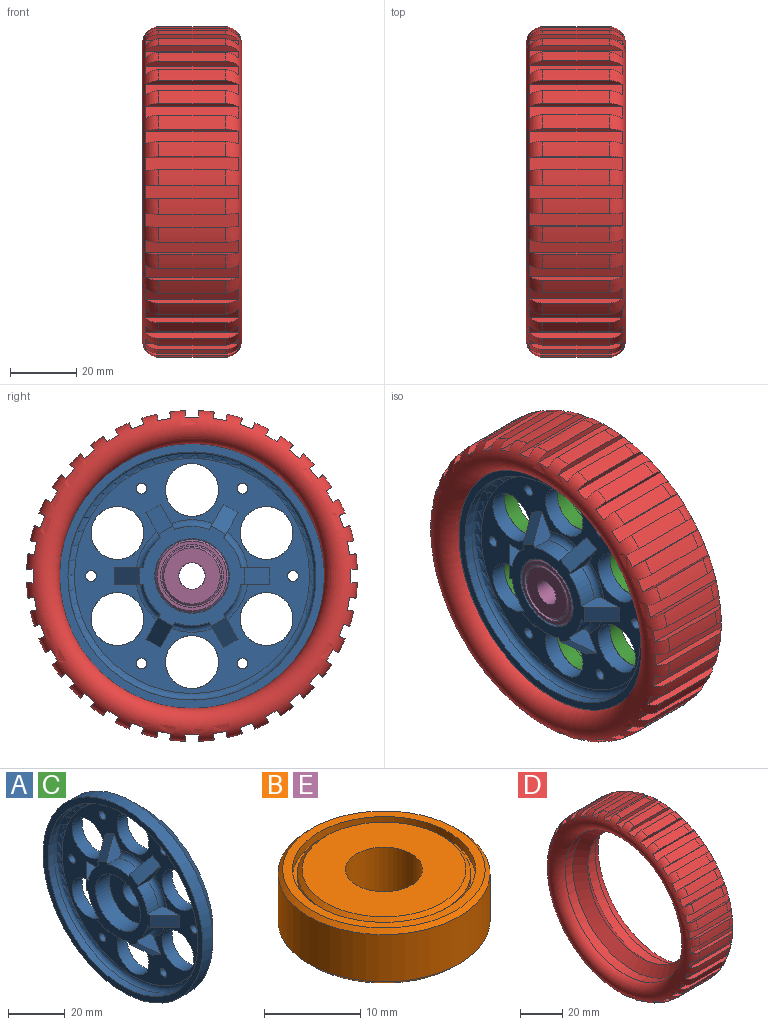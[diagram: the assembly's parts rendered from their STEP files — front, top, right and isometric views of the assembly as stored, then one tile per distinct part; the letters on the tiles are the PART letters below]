
ASSEMBLY  parts=5 mates=4
PART A: 53 faces, bbox 12.5x81.2x81.2 mm
  f0: cylinder r=15mm len=10.46mm, axis (-1,0,0), area 58.8mm2, adj f8,f15,f16,f17
  f1: cylinder r=15mm len=9.06mm, axis (-1,0,0), area 58.8mm2, adj f8,f19,f20,f21
  f2: cylinder r=15mm len=9.06mm, axis (-1,0,0), area 58.8mm2, adj f8,f23,f24,f25
  f3: cylinder r=15mm len=10.46mm, axis (-1,0,0), area 58.8mm2, adj f8,f27,f28,f29
  f4: cylinder r=15mm len=9.06mm, axis (-1,0,0), area 58.8mm2, adj f8,f31,f32,f33
  f5: cylinder r=11.25mm len=22.5mm, axis (-1,0,0), area 494.8mm2, adj f6,f8
  f6: plane 22.5x22.5mm, normal (-1,0,0), area 334mm2, adj f5,f7
  f7: cylinder r=4.5mm len=9mm, axis (-1,0,0), area 155.5mm2, adj f6,f52
  f8: plane 32x30.21mm, normal (-1,0,0), area 341.3mm2, adj f0,f1,f2,f3,f4,f5,f9,f14
  f9: cylinder r=15mm len=9.06mm, axis (-1,0,0), area 58.8mm2, adj f8,f35,f36,f37
  f10: plane 80x80mm, normal (-1,0,0), area 608.7mm2, adj f11,f13
  f11: cylinder r=40mm len=80mm, axis (-1,0,0), area 1256.6mm2, adj f10,f12
  f12: cone r=35mm half-angle=45deg, axis (-1,0,0), area 1666.1mm2, adj f11,f52
  f13: cylinder r=37.5mm len=75mm, axis (-1,0,0), area 706.9mm2, adj f10,f38
  f14: plane 9x8.08mm, normal (-0.71,-0.35,0.61), area 53mm2, adj f8,f15,f37,f50
  f15: plane 7.54x7.5mm, normal (0,0.87,0.5), area 36.3mm2, adj f0,f8,f14,f16,f50
  f16: torus R=17mm, axis (1,0,0), area 36mm2, adj f0,f15,f17,f50
  f17: plane 7.54x7.5mm, normal (0,-0.87,0.5), area 36.3mm2, adj f0,f8,f16,f18,f50
  f18: plane 9x8.08mm, normal (-0.71,0.35,0.61), area 53mm2, adj f8,f17,f19,f50
  f19: plane 7.54x7.5mm, normal (0,0.87,-0.5), area 36.3mm2, adj f1,f8,f18,f20,f50
  f20: torus R=17mm, axis (1,0,0), area 36mm2, adj f1,f19,f21,f50
  f21: plane 8.71x7.5mm, normal (0,0,1), area 36.3mm2, adj f1,f8,f20,f22,f50
  f22: plane 7.5x7.5mm, normal (-0.71,0.71,0), area 53mm2, adj f8,f21,f23,f50
  f23: plane 8.71x7.5mm, normal (0,0,-1), area 36.3mm2, adj f2,f8,f22,f24,f50
  f24: torus R=17mm, axis (1,0,0), area 36mm2, adj f2,f23,f25,f50
  f25: plane 7.54x7.5mm, normal (0,0.87,0.5), area 36.3mm2, adj f2,f8,f24,f26,f50
  f26: plane 9x8.08mm, normal (-0.71,0.35,-0.61), area 53mm2, adj f8,f25,f27,f50
  f27: plane 7.54x7.5mm, normal (0,-0.87,-0.5), area 36.3mm2, adj f3,f8,f26,f28,f50
  f28: torus R=17mm, axis (1,0,0), area 36mm2, adj f3,f27,f29,f50
  f29: plane 7.54x7.5mm, normal (0,0.87,-0.5), area 36.3mm2, adj f3,f8,f28,f30,f50
  f30: plane 9x8.08mm, normal (-0.71,-0.35,-0.61), area 53mm2, adj f8,f29,f31,f50
  f31: plane 7.54x7.5mm, normal (0,-0.87,0.5), area 36.3mm2, adj f4,f8,f30,f32,f50
  f32: torus R=17mm, axis (1,0,0), area 36mm2, adj f4,f31,f33,f50
  f33: plane 8.71x7.5mm, normal (0,0,-1), area 36.3mm2, adj f4,f8,f32,f34,f50
  f34: plane 7.5x7.5mm, normal (-0.71,-0.71,0), area 53mm2, adj f8,f33,f35,f50
  f35: plane 8.71x7.5mm, normal (0,0,1), area 36.3mm2, adj f8,f9,f34,f36,f50
  f36: torus R=17mm, axis (1,0,0), area 36mm2, adj f9,f35,f37,f50
  f37: plane 7.54x7.5mm, normal (0,-0.87,-0.5), area 36.3mm2, adj f8,f9,f14,f36,f50
  f38: torus R=35.5mm, axis (1,0,0), area 725.9mm2, adj f13,f50
  f39: cylinder r=8mm len=16mm, axis (-1,0,0), area 251.3mm2, adj f50,f52
  f40: cylinder r=8mm len=16mm, axis (-1,0,0), area 251.3mm2, adj f50,f52
  f41: cylinder r=8mm len=16mm, axis (-1,0,0), area 251.3mm2, adj f50,f52
  f42: cylinder r=8mm len=16mm, axis (-1,0,0), area 251.3mm2, adj f50,f52
  f43: cylinder r=8mm len=16mm, axis (-1,0,0), area 251.3mm2, adj f50,f52
  f44: cylinder r=8mm len=16mm, axis (-1,0,0), area 251.3mm2, adj f50,f52
  f45: cylinder r=1.65mm len=5mm, axis (1,0,0), area 51.8mm2, adj f50,f52
  f46: cylinder r=1.65mm len=5mm, axis (1,0,0), area 51.8mm2, adj f50,f52
  f47: cylinder r=1.65mm len=5mm, axis (1,0,0), area 51.8mm2, adj f50,f52
  f48: cylinder r=1.65mm len=5mm, axis (1,0,0), area 51.8mm2, adj f50,f52
  f49: cylinder r=1.65mm len=5mm, axis (1,0,0), area 51.8mm2, adj f50,f52
  f50: plane 71x71mm, normal (-1,0,0), area 1596.7mm2, adj f14,f15,f16,f17,f18,f19,f20,f21
  f51: cylinder r=1.65mm len=5mm, axis (1,0,0), area 51.8mm2, adj f50,f52
  f52: plane 70x70mm, normal (1,0,0), area 2527.1mm2, adj f7,f12,f39,f40,f41,f42,f43,f44
PART B: 16 faces, bbox 22x22x7 mm
  f0: cone r=8.5mm half-angle=45deg, axis (0,0,1), area 38.9mm2, adj f1,f15
  f1: plane 17x17mm, normal (0,0,-1), area 176.7mm2, adj f0,f2
  f2: cylinder r=4mm len=8mm, axis (0,0,-1), area 175.9mm2, adj f1,f3
  f3: plane 17x17mm, normal (0,0,1), area 176.7mm2, adj f2,f4
  f4: cone r=8.5mm half-angle=45deg, axis (0,0,-1), area 38.9mm2, adj f3,f5
  f5: cylinder r=9mm len=18mm, axis (0,0,-1), area 28.3mm2, adj f4,f6
  f6: plane 19x19mm, normal (0,0,1), area 29.1mm2, adj f5,f7
  f7: cylinder r=9.5mm len=19mm, axis (0,0,-1), area 59.7mm2, adj f6,f8
  f8: plane 21x21mm, normal (0,0,1), area 62.8mm2, adj f7,f9
  f9: cone r=10.5mm half-angle=45deg, axis (0,0,-1), area 47.8mm2, adj f8,f10
  f10: cylinder r=11mm len=22mm, axis (0,0,-1), area 414.7mm2, adj f9,f11
  f11: cone r=10.5mm half-angle=45deg, axis (0,0,1), area 47.8mm2, adj f10,f12
  f12: plane 21x21mm, normal (0,0,-1), area 62.8mm2, adj f11,f13
  f13: cylinder r=9.5mm len=19mm, axis (0,0,-1), area 59.7mm2, adj f12,f14
  f14: plane 19x19mm, normal (0,0,-1), area 29.1mm2, adj f13,f15
  f15: cylinder r=9mm len=18mm, axis (0,0,-1), area 28.3mm2, adj f0,f14
PART C: same geometry as A
PART D: 150 faces, bbox 30.1x108.3x108.3 mm
  f0: torus R=45mm, axis (1,0,0), area 3776.6mm2, adj f1,f2,f3,f4,f5,f6,f7,f8
  f1: cylinder r=50mm len=20mm, axis (1,0,0), area 94.5mm2, adj f0,f37,f144,f149
  f2: cylinder r=50mm len=20mm, axis (1,0,0), area 94.5mm2, adj f0,f37,f141,f146
  f3: cylinder r=50mm len=20mm, axis (1,0,0), area 94.5mm2, adj f0,f37,f138,f143
  f4: cylinder r=50mm len=20mm, axis (1,0,0), area 94.5mm2, adj f0,f37,f135,f140
  f5: cylinder r=50mm len=20mm, axis (1,0,0), area 94.5mm2, adj f0,f37,f132,f137
  f6: cylinder r=50mm len=20mm, axis (1,0,0), area 94.5mm2, adj f0,f37,f129,f134
  f7: cylinder r=50mm len=20mm, axis (1,0,0), area 94.5mm2, adj f0,f37,f126,f131
  f8: cylinder r=50mm len=20mm, axis (1,0,0), area 94.5mm2, adj f0,f37,f123,f128
  f9: cylinder r=50mm len=20mm, axis (1,0,0), area 94.5mm2, adj f0,f37,f120,f125
  f10: cylinder r=50mm len=20mm, axis (1,0,0), area 94.5mm2, adj f0,f37,f117,f122
  f11: cylinder r=50mm len=20mm, axis (1,0,0), area 94.5mm2, adj f0,f37,f114,f119
  f12: cylinder r=50mm len=20mm, axis (1,0,0), area 94.5mm2, adj f0,f37,f111,f116
  f13: cylinder r=50mm len=20mm, axis (1,0,0), area 94.5mm2, adj f0,f37,f108,f113
  f14: cylinder r=50mm len=20mm, axis (1,0,0), area 94.5mm2, adj f0,f37,f105,f110
  f15: cylinder r=50mm len=20mm, axis (1,0,0), area 94.5mm2, adj f0,f37,f102,f107
  f16: cylinder r=50mm len=20mm, axis (1,0,0), area 94.5mm2, adj f0,f37,f99,f104
  f17: cylinder r=50mm len=20mm, axis (1,0,0), area 94.5mm2, adj f0,f37,f96,f101
  f18: cylinder r=50mm len=20mm, axis (1,0,0), area 94.5mm2, adj f0,f37,f93,f98
  f19: cylinder r=50mm len=20mm, axis (1,0,0), area 94.5mm2, adj f0,f37,f90,f95
  f20: cylinder r=50mm len=20mm, axis (1,0,0), area 94.5mm2, adj f0,f37,f87,f92
  f21: cylinder r=50mm len=20mm, axis (1,0,0), area 94.5mm2, adj f0,f37,f84,f89
  f22: cylinder r=50mm len=20mm, axis (1,0,0), area 94.5mm2, adj f0,f37,f81,f86
  f23: cylinder r=50mm len=20mm, axis (1,0,0), area 94.5mm2, adj f0,f37,f78,f83
  f24: cylinder r=50mm len=20mm, axis (1,0,0), area 94.5mm2, adj f0,f37,f75,f80
  f25: cylinder r=50mm len=20mm, axis (1,0,0), area 94.5mm2, adj f0,f37,f72,f77
  f26: cylinder r=50mm len=20mm, axis (1,0,0), area 94.5mm2, adj f0,f37,f69,f74
  f27: cylinder r=50mm len=20mm, axis (1,0,0), area 94.5mm2, adj f0,f37,f66,f71
  f28: cylinder r=50mm len=20mm, axis (1,0,0), area 94.5mm2, adj f0,f37,f63,f68
  f29: cylinder r=50mm len=20mm, axis (1,0,0), area 94.5mm2, adj f0,f37,f60,f65
  f30: cylinder r=50mm len=20mm, axis (1,0,0), area 94.5mm2, adj f0,f37,f57,f62
  f31: cylinder r=50mm len=20mm, axis (1,0,0), area 94.5mm2, adj f0,f37,f54,f59
  f32: cylinder r=50mm len=20mm, axis (1,0,0), area 94.5mm2, adj f0,f37,f44,f56
  f33: cylinder r=50mm len=20mm, axis (1,0,0), area 94.5mm2, adj f0,f37,f53,f147
  f34: cylinder r=50mm len=20mm, axis (1,0,0), area 94.5mm2, adj f0,f37,f50,f51
  f35: cylinder r=50mm len=20mm, axis (1,0,0), area 94.5mm2, adj f0,f37,f47,f48
  f36: cylinder r=50mm len=20mm, axis (1,0,0), area 94.5mm2, adj f0,f37,f43,f45
  f37: torus R=45mm, axis (1,0,0), area 3776.6mm2, adj f1,f2,f3,f4,f5,f6,f7,f8
  f38: cylinder r=40mm len=80mm, axis (1,0,0), area 1256.6mm2, adj f37,f39
  f39: cone r=35mm half-angle=45deg, axis (-1,0,0), area 1666.1mm2, adj f38,f40
  f40: cone r=40mm half-angle=45deg, axis (1,0,0), area 1666.1mm2, adj f39,f41
  f41: cylinder r=40mm len=80mm, axis (1,0,0), area 1256.6mm2, adj f0,f40
  f42: plane 28.11x4.11mm, normal (0,0,1), area 111.9mm2, adj f0,f37,f43,f44
  f43: plane 27.98x2.01mm, normal (0,-1,0), area 50.1mm2, adj f0,f36,f37,f42
  f44: plane 27.98x2.01mm, normal (0,1,0), area 50.1mm2, adj f0,f32,f37,f42
  f45: plane 27.98x1.97mm, normal (0,0.98,-0.17), area 50.1mm2, adj f0,f36,f37,f46
  f46: plane 28.1x4.04mm, normal (0,0.17,0.98), area 111.9mm2, adj f0,f37,f45,f47
  f47: plane 27.98x1.97mm, normal (0,-0.98,0.17), area 50.1mm2, adj f0,f35,f37,f46
  f48: plane 27.98x1.88mm, normal (0,0.94,-0.34), area 50.1mm2, adj f0,f35,f37,f49
  f49: plane 28.1x3.86mm, normal (0,0.34,0.94), area 111.9mm2, adj f0,f37,f48,f50
  f50: plane 27.98x1.88mm, normal (0,-0.94,0.34), area 50.1mm2, adj f0,f34,f37,f49
  f51: plane 27.98x1.74mm, normal (0,0.87,-0.5), area 50.1mm2, adj f0,f34,f37,f52
  f52: plane 28.1x3.57mm, normal (0,0.5,0.87), area 111.9mm2, adj f0,f37,f51,f53
  f53: plane 27.98x1.74mm, normal (0,-0.87,0.5), area 50.1mm2, adj f0,f33,f37,f52
  f54: plane 27.98x1.97mm, normal (0,0.98,0.17), area 50.1mm2, adj f0,f31,f37,f55
  f55: plane 28.1x4.04mm, normal (0,-0.17,0.98), area 111.9mm2, adj f0,f37,f54,f56
  f56: plane 27.98x1.97mm, normal (0,-0.98,-0.17), area 50.1mm2, adj f0,f32,f37,f55
  f57: plane 27.98x1.88mm, normal (0,0.94,0.34), area 50.1mm2, adj f0,f30,f37,f58
  f58: plane 28.1x3.86mm, normal (0,-0.34,0.94), area 111.9mm2, adj f0,f37,f57,f59
  f59: plane 27.98x1.88mm, normal (0,-0.94,-0.34), area 50.1mm2, adj f0,f31,f37,f58
  f60: plane 27.98x1.74mm, normal (0,0.87,0.5), area 50.1mm2, adj f0,f29,f37,f61
  f61: plane 28.1x3.57mm, normal (0,-0.5,0.87), area 111.9mm2, adj f0,f37,f60,f62
  f62: plane 27.98x1.74mm, normal (0,-0.87,-0.5), area 50.1mm2, adj f0,f30,f37,f61
  f63: plane 27.98x1.54mm, normal (0,0.77,0.64), area 50.1mm2, adj f0,f28,f37,f64
  f64: plane 28.1x3.17mm, normal (0,-0.64,0.77), area 111.9mm2, adj f0,f37,f63,f65
  f65: plane 27.98x1.54mm, normal (0,-0.77,-0.64), area 50.1mm2, adj f0,f29,f37,f64
  f66: plane 27.98x1.54mm, normal (0,0.64,0.77), area 50.1mm2, adj f0,f27,f37,f67
  f67: plane 28.1x3.17mm, normal (0,-0.77,0.64), area 111.9mm2, adj f0,f37,f66,f68
  f68: plane 27.98x1.54mm, normal (0,-0.64,-0.77), area 50.1mm2, adj f0,f28,f37,f67
  f69: plane 27.98x1.74mm, normal (0,0.5,0.87), area 50.1mm2, adj f0,f26,f37,f70
  f70: plane 28.1x3.57mm, normal (0,-0.87,0.5), area 111.9mm2, adj f0,f37,f69,f71
  f71: plane 27.98x1.74mm, normal (0,-0.5,-0.87), area 50.1mm2, adj f0,f27,f37,f70
  f72: plane 27.98x1.88mm, normal (0,0.34,0.94), area 50.1mm2, adj f0,f25,f37,f73
  f73: plane 28.1x3.86mm, normal (0,-0.94,0.34), area 111.9mm2, adj f0,f37,f72,f74
  f74: plane 27.98x1.88mm, normal (0,-0.34,-0.94), area 50.1mm2, adj f0,f26,f37,f73
  f75: plane 27.98x1.97mm, normal (0,0.17,0.98), area 50.1mm2, adj f0,f24,f37,f76
  f76: plane 28.1x4.04mm, normal (0,-0.98,0.17), area 111.9mm2, adj f0,f37,f75,f77
  f77: plane 27.98x1.97mm, normal (0,-0.17,-0.98), area 50.1mm2, adj f0,f25,f37,f76
  f78: plane 27.98x2.01mm, normal (0,0,1), area 50.1mm2, adj f0,f23,f37,f79
  f79: plane 28.11x4.11mm, normal (0,-1,0), area 111.9mm2, adj f0,f37,f78,f80
  f80: plane 27.98x2.01mm, normal (0,0,-1), area 50.1mm2, adj f0,f24,f37,f79
  f81: plane 27.98x1.97mm, normal (0,-0.17,0.98), area 50.1mm2, adj f0,f22,f37,f82
  f82: plane 28.1x4.04mm, normal (0,-0.98,-0.17), area 111.9mm2, adj f0,f37,f81,f83
  f83: plane 27.98x1.97mm, normal (0,0.17,-0.98), area 50.1mm2, adj f0,f23,f37,f82
  f84: plane 27.98x1.88mm, normal (0,-0.34,0.94), area 50.1mm2, adj f0,f21,f37,f85
  f85: plane 28.1x3.86mm, normal (0,-0.94,-0.34), area 111.9mm2, adj f0,f37,f84,f86
  f86: plane 27.98x1.88mm, normal (0,0.34,-0.94), area 50.1mm2, adj f0,f22,f37,f85
  f87: plane 27.98x1.74mm, normal (0,-0.5,0.87), area 50.1mm2, adj f0,f20,f37,f88
  f88: plane 28.1x3.57mm, normal (0,-0.87,-0.5), area 111.9mm2, adj f0,f37,f87,f89
  f89: plane 27.98x1.74mm, normal (0,0.5,-0.87), area 50.1mm2, adj f0,f21,f37,f88
  f90: plane 27.98x1.54mm, normal (0,-0.64,0.77), area 50.1mm2, adj f0,f19,f37,f91
  f91: plane 28.1x3.17mm, normal (0,-0.77,-0.64), area 111.9mm2, adj f0,f37,f90,f92
  f92: plane 27.98x1.54mm, normal (0,0.64,-0.77), area 50.1mm2, adj f0,f20,f37,f91
  f93: plane 27.98x1.54mm, normal (0,-0.77,0.64), area 50.1mm2, adj f0,f18,f37,f94
  f94: plane 28.1x3.17mm, normal (0,-0.64,-0.77), area 111.9mm2, adj f0,f37,f93,f95
  f95: plane 27.98x1.54mm, normal (0,0.77,-0.64), area 50.1mm2, adj f0,f19,f37,f94
  f96: plane 27.98x1.74mm, normal (0,-0.87,0.5), area 50.1mm2, adj f0,f17,f37,f97
  f97: plane 28.1x3.57mm, normal (0,-0.5,-0.87), area 111.9mm2, adj f0,f37,f96,f98
  f98: plane 27.98x1.74mm, normal (0,0.87,-0.5), area 50.1mm2, adj f0,f18,f37,f97
  f99: plane 27.98x1.88mm, normal (0,-0.94,0.34), area 50.1mm2, adj f0,f16,f37,f100
  f100: plane 28.1x3.86mm, normal (0,-0.34,-0.94), area 111.9mm2, adj f0,f37,f99,f101
  f101: plane 27.98x1.88mm, normal (0,0.94,-0.34), area 50.1mm2, adj f0,f17,f37,f100
  f102: plane 27.98x1.97mm, normal (0,-0.98,0.17), area 50.1mm2, adj f0,f15,f37,f103
  f103: plane 28.1x4.04mm, normal (0,-0.17,-0.98), area 111.9mm2, adj f0,f37,f102,f104
  f104: plane 27.98x1.97mm, normal (0,0.98,-0.17), area 50.1mm2, adj f0,f16,f37,f103
  f105: plane 27.98x2.01mm, normal (0,-1,0), area 50.1mm2, adj f0,f14,f37,f106
  f106: plane 28.03x4.03mm, normal (0,0,-1), area 111.9mm2, adj f0,f37,f105,f107
  f107: plane 27.98x2.01mm, normal (0,1,0), area 50.1mm2, adj f0,f15,f37,f106
  f108: plane 27.98x1.97mm, normal (0,-0.98,-0.17), area 50.1mm2, adj f0,f13,f37,f109
  f109: plane 28.1x4.04mm, normal (0,0.17,-0.98), area 111.9mm2, adj f0,f37,f108,f110
  f110: plane 27.98x1.97mm, normal (0,0.98,0.17), area 50.1mm2, adj f0,f14,f37,f109
  f111: plane 27.98x1.88mm, normal (0,-0.94,-0.34), area 50.1mm2, adj f0,f12,f37,f112
  f112: plane 28.1x3.86mm, normal (0,0.34,-0.94), area 111.9mm2, adj f0,f37,f111,f113
  f113: plane 27.98x1.88mm, normal (0,0.94,0.34), area 50.1mm2, adj f0,f13,f37,f112
  f114: plane 27.98x1.74mm, normal (0,-0.87,-0.5), area 50.1mm2, adj f0,f11,f37,f115
  f115: plane 28.1x3.57mm, normal (0,0.5,-0.87), area 111.9mm2, adj f0,f37,f114,f116
  f116: plane 27.98x1.74mm, normal (0,0.87,0.5), area 50.1mm2, adj f0,f12,f37,f115
  f117: plane 27.98x1.54mm, normal (0,-0.77,-0.64), area 50.1mm2, adj f0,f10,f37,f118
  f118: plane 28.1x3.17mm, normal (0,0.64,-0.77), area 111.9mm2, adj f0,f37,f117,f119
  f119: plane 27.98x1.54mm, normal (0,0.77,0.64), area 50.1mm2, adj f0,f11,f37,f118
  f120: plane 27.98x1.54mm, normal (0,-0.64,-0.77), area 50.1mm2, adj f0,f9,f37,f121
  f121: plane 28.1x3.17mm, normal (0,0.77,-0.64), area 111.9mm2, adj f0,f37,f120,f122
  f122: plane 27.98x1.54mm, normal (0,0.64,0.77), area 50.1mm2, adj f0,f10,f37,f121
  f123: plane 27.98x1.74mm, normal (0,-0.5,-0.87), area 50.1mm2, adj f0,f8,f37,f124
  f124: plane 28.1x3.57mm, normal (0,0.87,-0.5), area 111.9mm2, adj f0,f37,f123,f125
  f125: plane 27.98x1.74mm, normal (0,0.5,0.87), area 50.1mm2, adj f0,f9,f37,f124
  f126: plane 27.98x1.88mm, normal (0,-0.34,-0.94), area 50.1mm2, adj f0,f7,f37,f127
  f127: plane 28.1x3.86mm, normal (0,0.94,-0.34), area 111.9mm2, adj f0,f37,f126,f128
  f128: plane 27.98x1.88mm, normal (0,0.34,0.94), area 50.1mm2, adj f0,f8,f37,f127
  f129: plane 27.98x1.97mm, normal (0,-0.17,-0.98), area 50.1mm2, adj f0,f6,f37,f130
  f130: plane 28.1x4.04mm, normal (0,0.98,-0.17), area 111.9mm2, adj f0,f37,f129,f131
  f131: plane 27.98x1.97mm, normal (0,0.17,0.98), area 50.1mm2, adj f0,f7,f37,f130
  f132: plane 27.98x2.01mm, normal (0,0,-1), area 50.1mm2, adj f0,f5,f37,f133
  f133: plane 28.11x4.11mm, normal (0,1,0), area 111.9mm2, adj f0,f37,f132,f134
  f134: plane 27.98x2.01mm, normal (0,0,1), area 50.1mm2, adj f0,f6,f37,f133
  f135: plane 27.98x1.97mm, normal (0,0.17,-0.98), area 50.1mm2, adj f0,f4,f37,f136
  f136: plane 28.1x4.04mm, normal (0,0.98,0.17), area 111.9mm2, adj f0,f37,f135,f137
  f137: plane 27.98x1.97mm, normal (0,-0.17,0.98), area 50.1mm2, adj f0,f5,f37,f136
  f138: plane 27.98x1.88mm, normal (0,0.34,-0.94), area 50.1mm2, adj f0,f3,f37,f139
  f139: plane 28.1x3.86mm, normal (0,0.94,0.34), area 111.9mm2, adj f0,f37,f138,f140
  f140: plane 27.98x1.88mm, normal (0,-0.34,0.94), area 50.1mm2, adj f0,f4,f37,f139
  f141: plane 27.98x1.74mm, normal (0,0.5,-0.87), area 50.1mm2, adj f0,f2,f37,f142
  f142: plane 28.1x3.57mm, normal (0,0.87,0.5), area 111.9mm2, adj f0,f37,f141,f143
  f143: plane 27.98x1.74mm, normal (0,-0.5,0.87), area 50.1mm2, adj f0,f3,f37,f142
  f144: plane 27.98x1.54mm, normal (0,0.64,-0.77), area 50.1mm2, adj f0,f1,f37,f145
  f145: plane 28.1x3.17mm, normal (0,0.77,0.64), area 111.9mm2, adj f0,f37,f144,f146
  f146: plane 27.98x1.54mm, normal (0,-0.64,0.77), area 50.1mm2, adj f0,f2,f37,f145
  f147: plane 27.98x1.54mm, normal (0,0.77,-0.64), area 50.1mm2, adj f0,f33,f37,f148
  f148: plane 28.1x3.17mm, normal (0,0.64,0.77), area 111.9mm2, adj f0,f37,f147,f149
  f149: plane 27.98x1.54mm, normal (0,-0.77,0.64), area 50.1mm2, adj f0,f1,f37,f148
PART E: same geometry as B
PLACE A rot(axis=(-0.82,-0.47,-0.33),0deg) t=(-18.07,-25.96,51.78)mm
PLACE B rot(axis=(0.71,0,-0.71),180deg) t=(-9.07,-25.96,51.78)mm
PLACE C rot(axis=(0,1,0),180deg) t=(-18.07,-25.96,51.78)mm
PLACE D rot(axis=(-0.82,-0.47,-0.33),0deg) t=(-18.07,-25.96,51.78)mm
PLACE E rot(axis=(0.71,0,0.71),180deg) t=(-27.07,-25.96,51.78)mm
MATE fastened C.f0 <-> A.f0  axis (-1,0,0) through (-18.07,-25.96,51.78)mm
MATE revolute B.f0 <-> A.f0  axis (-1,0,0) through (-12.57,-25.96,51.78)mm
MATE fastened D.f0 <-> A.f0  axis (1,0,0) through (-18.07,-25.96,51.78)mm
MATE revolute E.f0 <-> A.f0  axis (1,0,0) through (-23.57,-25.96,51.78)mm
